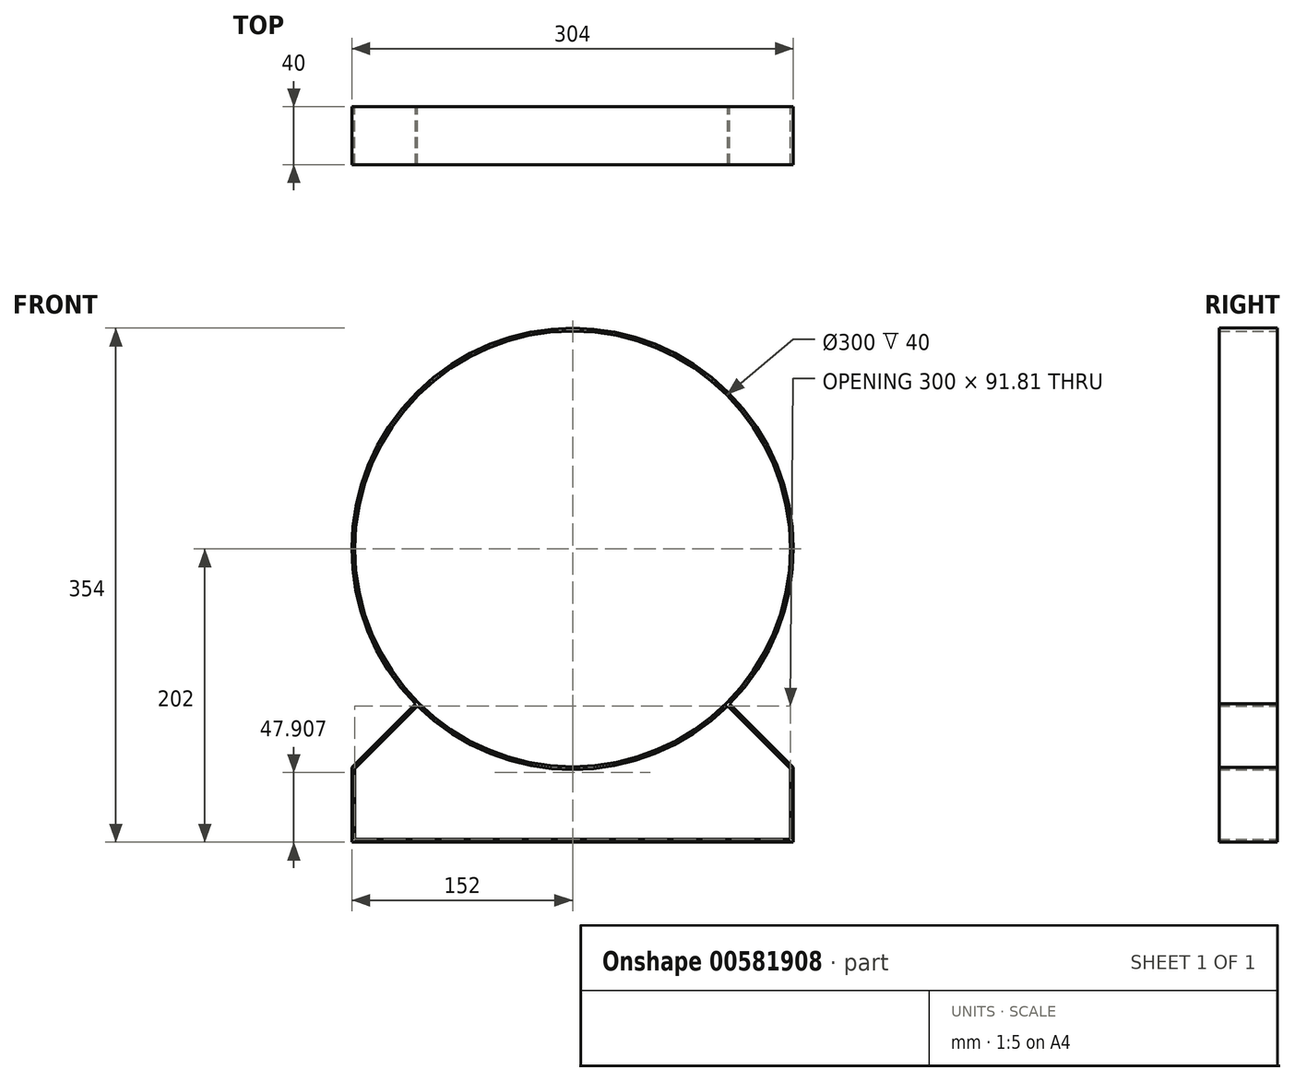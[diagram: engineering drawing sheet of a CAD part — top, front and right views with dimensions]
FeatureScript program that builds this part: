
annotation { "Feature Type Name" : "Feature", "Feature Type Description" : "" }
export const myFeature = defineFeature(function(context is Context, id is Id, definition is map)
    precondition{}
    {
        {
            var Q0;
            Q0=qCreatedBy(makeId("Front.planeOp"),FACE);
            var sketch = newSketch(context, id + "F0", { "sketchPlane" : qUnion([Q0])});
            skLineSegment(sketch, "E0", {"start": v(0, 0) * mm, "end": v(-679.96, 0) * mm, "construction": true});
            skLineSegment(sketch, "E1", {"start": v(0, 0) * mm, "end": v(0, 658.78) * mm, "construction": true});
            skLineSegment(sketch, "E2", {"start": v(0, 0) * mm, "end": v(-291.77, -291.77) * mm, "construction": true});
            skLineSegment(sketch, "E3", {"start": v(0, 0) * mm, "end": v(291.77, -291.77) * mm, "construction": true});
            skCircle(sketch, "E4", {"center": v(0, 0) * mm, "radius": 150 * mm});
            skCircle(sketch, "E5", {"center": v(0, 0) * mm, "radius": 152 * mm});
            skLineSegment(sketch, "E6", {"start": v(-152, -202) * mm, "end": v(0, -202) * mm});
            skLineSegment(sketch, "E7", {"start": v(-150, -200) * mm, "end": v(0, -200) * mm});
            skLineSegment(sketch, "E8", {"start": v(0, 0) * mm, "end": v(0, -311.11) * mm, "construction": true});
            skLineSegment(sketch, "E9", {"start": v(-150, -200) * mm, "end": v(-150, -151.41) * mm});
            skLineSegment(sketch, "E10", {"start": v(-152, -202) * mm, "end": v(-152, -150.59) * mm});
            skLineSegment(sketch, "E11", {"start": v(-108.19, -106.77) * mm, "end": v(-152, -150.59) * mm});
            skLineSegment(sketch, "E12", {"start": v(-106.77, -108.19) * mm, "end": v(-150, -151.41) * mm});
            skLineSegment(sketch, "E13.MirrorCS", {"start": v(106.77, -108.19) * mm, "end": v(150, -151.41) * mm});
            skLineSegment(sketch, "E14.MirrorCS", {"start": v(152, -202) * mm, "end": v(0, -202) * mm});
            skLineSegment(sketch, "E15.MirrorCS", {"start": v(150, -200) * mm, "end": v(0, -200) * mm});
            skLineSegment(sketch, "E16.MirrorCS", {"start": v(108.19, -106.77) * mm, "end": v(152, -150.59) * mm});
            skLineSegment(sketch, "E17.MirrorCS", {"start": v(150, -200) * mm, "end": v(150, -151.41) * mm});
            skLineSegment(sketch, "E18.MirrorCS", {"start": v(152, -202) * mm, "end": v(152, -150.59) * mm});
            skSolve(sketch);
        }
        {
            var Q0;
            Q0=qSketchRegion(id+"F0",true);
            extrude(context, id + "F1", {"entities" : qUnion([Q0]), "offsetDistance" : 25 * mm, "depth" : 40 * mm});
        }
    });
